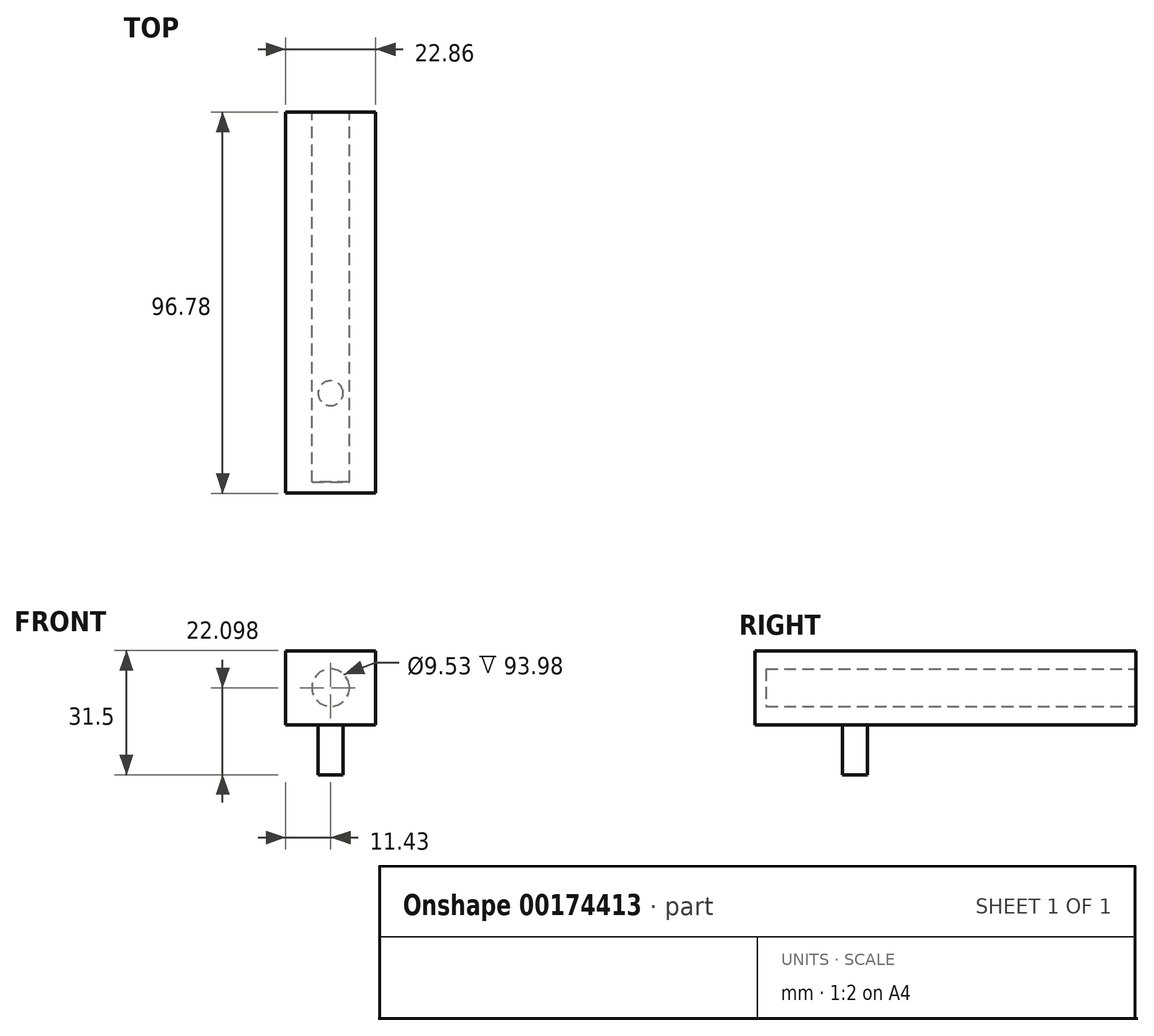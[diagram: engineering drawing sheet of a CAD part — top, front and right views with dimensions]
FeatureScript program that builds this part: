
annotation { "Feature Type Name" : "Feature", "Feature Type Description" : "" }
export const myFeature = defineFeature(function(context is Context, id is Id, definition is map)
    precondition{}
    {
        {
            var Q0;
            Q0=qCreatedBy(makeId("Top.planeOp"),FACE);
            var sketch = newSketch(context, id + "F0", { "sketchPlane" : qUnion([Q0])});
            skLineSegment(sketch, "E0.bottom", {"start": v(11.43, 48.39) * mm, "end": v(-11.43, 48.39) * mm});
            skLineSegment(sketch, "E0.top", {"start": v(11.43, -48.39) * mm, "end": v(-11.43, -48.39) * mm});
            skLineSegment(sketch, "E0.left", {"start": v(11.43, 48.39) * mm, "end": v(11.43, -48.39) * mm});
            skLineSegment(sketch, "E0.right", {"start": v(-11.43, 48.39) * mm, "end": v(-11.43, -48.39) * mm});
            skPoint(sketch, "E0.middle", {"position": v(0, 0) * mm});
            skSolve(sketch);
        }
        {
            var Q0;
            Q0 = qSketchRegion(id + "F0", true);
            extrude(context, id + "F1", {"entities" : qUnion([Q0]), "depth" : 18.8 * mm, "offsetDistance" : 25.4 * mm});
        }
        {
            var Q0;
            Q0=makeQuery(id+"F1.opExtrude","SWEPT_FACE",FACE,{"disambiguationData":[OSD([sQuery(id+"F0.wireOp",EDGE,"E0.bottom")])]});
            var sketch = newSketch(context, id + "F2", { "sketchPlane" : qUnion([Q0])});
            skCircle(sketch, "E1", {"center": v(0, 9.4) * mm, "radius": 4.76 * mm});
            skPoint(sketch, "E1.centerSnap0", {"position": v(-11.43, 9.4) * mm});
            skSolve(sketch);
        }
        {
            var Q0;
            Q0 = qSketchRegion(id + "F2", true);
            extrude(context, id + "F3", {"entities" : qUnion([Q0]), "operationType" : NewBodyOperationType.REMOVE, "oppositeDirection" : true, "depth" : 93.98 * mm, "offsetDistance" : 25.4 * mm});
        }
        {
            var Q0;
            Q0=makeQuery(id+"F1.opExtrude","CAP_FACE",FACE,{"disambiguationData":[OSD([sQuery(id+"F0.wireOp",EDGE,"E0.bottom"),sQuery(id+"F0.wireOp",EDGE,"E0.top"),sQuery(id+"F0.wireOp",EDGE,"E0.left"),sQuery(id+"F0.wireOp",EDGE,"E0.right")])],"isStart":true});
            var sketch = newSketch(context, id + "F4", { "sketchPlane" : qUnion([Q0])});
            skCircle(sketch, "E2", {"center": v(0, 22.99) * mm, "radius": 3.18 * mm});
            skSolve(sketch);
        }
        {
            var Q0;
            Q0 = qSketchRegion(id + "F4", true);
            extrude(context, id + "F5", {"entities" : qUnion([Q0]), "operationType" : NewBodyOperationType.ADD, "depth" : 12.7 * mm, "offsetDistance" : 25.4 * mm});
        }
    });
